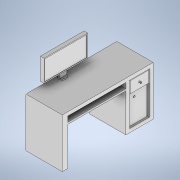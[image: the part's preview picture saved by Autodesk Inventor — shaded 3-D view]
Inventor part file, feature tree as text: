
AUTODESK INVENTOR PART (.ipt)
format: ipt  version: 2022 (Build 260153000, 153)  size: 520,192 bytes
history: native  units: mm
features: sketch x17, extrude x16, fillet x7, plane x2, shell x1, loft x1
ambient origin geometry x8: Origin, YZ Plane, XZ Plane, XY Plane, X Axis, Y Axis, Z Axis, Center Point
bodies: Solid1 (feature_tree)
feature tree (44):
  extrude  "Extrusion1"  Depth=10.0mm
  sketch  "Sketch2"  dims[d2=1.0mm d3=0.0mm d4=1.5mm]
  extrude  "Extrusion2"  Depth=1.5mm
  extrude  "Extrusion3"  Depth=7.5mm
  extrude  "Extrusion5"  Depth=25.0mm
  fillet  "Fillet1"  Radius=1.0mm
  shell  "Shell1"  Thickness=2.0mm
  extrude  "Extrusion6"  Depth=2.0mm
  extrude  "Extrusion7"  TaperAngle=0.0deg  [1 undecoded]
  fillet  "Fillet2"  Radius=7.0mm
  extrude  "Extrusion8"  Depth=0.1mm
  fillet  "Fillet3"  Radius=1.0mm
  sketch  "Sketch7"  dims[d20=0.0mm d21=0.0mm d22=0.1mm d23=1.0mm]
  plane  "Work Plane1"
  loft  "Loft1"
  fillet  "Fillet4"  [1 undecoded]
  fillet  "Fillet5"  Radius=8.0mm
  sketch  "Sketch9"  dims[d28=8.5mm d29=0.0mm d30=0.5mm]
  plane  "Work Plane2"
  sketch  "Sketch10"  dims[d31=1.5mm d32=1.5mm]
  extrude  "Extrusion9"  Depth=0.5mm
  extrude  "Extrusion10"  Depth=1.5mm
  extrude  "Extrusion11"  Depth=0.05mm
  extrude  "Extrusion12"  Depth=0.05mm
  extrude  "Extrusion13"  Depth=3.4mm
  extrude  "Extrusion14"  Depth=0.15mm
  extrude  "Extrusion15"  Depth=1.55mm
  extrude  "Extrusion16"  Depth=0.5mm
  fillet  "Fillet7"  Radius=0.5mm
  extrude  "Extrusion17"  TaperAngle=0.0deg  [1 undecoded]
  fillet  "Fillet8"  Radius=0.075mm
  sketch  "Sketch1"  dims[d0=25.0mm d1=10.0mm]
  sketch  "Sketch3"  dims[d5=10.0mm d6=7.5mm]
  sketch  "Sketch4"  dims[d7=10.0mm d8=25.0mm d9=1.0mm d10=2.0mm d11=0.0mm]
  sketch  "Sketch5"  dims[d12=12.5mm d13=0.0mm d16=2.0mm]
  sketch  "Sketch6"  dims[d17=0.5mm d18=0.0mm d19=7.0mm]
  sketch  "Sketch8"  dims[d24=5.0mm d25=0.25mm d26=0.0mm d27=8.0mm]
  sketch  "Sketch11"  dims[d33=0.1mm d34=0.0mm d35=0.05mm]
  sketch  "Sketch12"  dims[d36=5.4mm d37=0.05mm]
  sketch  "Sketch13"  dims[d38=0.05mm d39=3.4mm]
  sketch  "Sketch14"  dims[d40=9.0mm d41=0.0mm d42=0.15mm]
  sketch  "Sketch15"  dims[d43=0.3mm d44=1.55mm]
  sketch  "Sketch16"  dims[d45=2.55mm d46=0.5mm d47=0.5mm]
  sketch  "Sketch17"  dims[d48=0.0mm d49=90.0deg d50=0.0mm d51=90.0deg d52=0.075mm d53=0.075mm d54=-1.0mm d55=12.0mm d56=6.0mm d57=2.0mm d58=3.0mm d59=0.25mm d60=1.0mm d61=0.0mm d62=0.9mm d63=0.0mm d64=3.5mm d65=0.0mm d66=1.75mm d67=0.75mm d68=1.75mm d69=0.75mm d70=10.0mm d71=0.0mm d72=10.0mm d73=0.0mm d74=2.5mm d75=2.5mm d76=0.5mm d77=1.0mm d78=0.0mm d79=16.0mm d80=0.5mm d81=1.0mm d82=0.0mm d83=0.1mm d84=0.25mm d85=0.0mm d87=0.05mm d88=1.25mm d89=0.0mm d90=0.01mm d86=0.872665mm]
note: 3 required parameter values undecoded (feature->parameter linkage not recoverable at this tier; creation-order binding heuristic only, values carry confidence <= 0.55)
